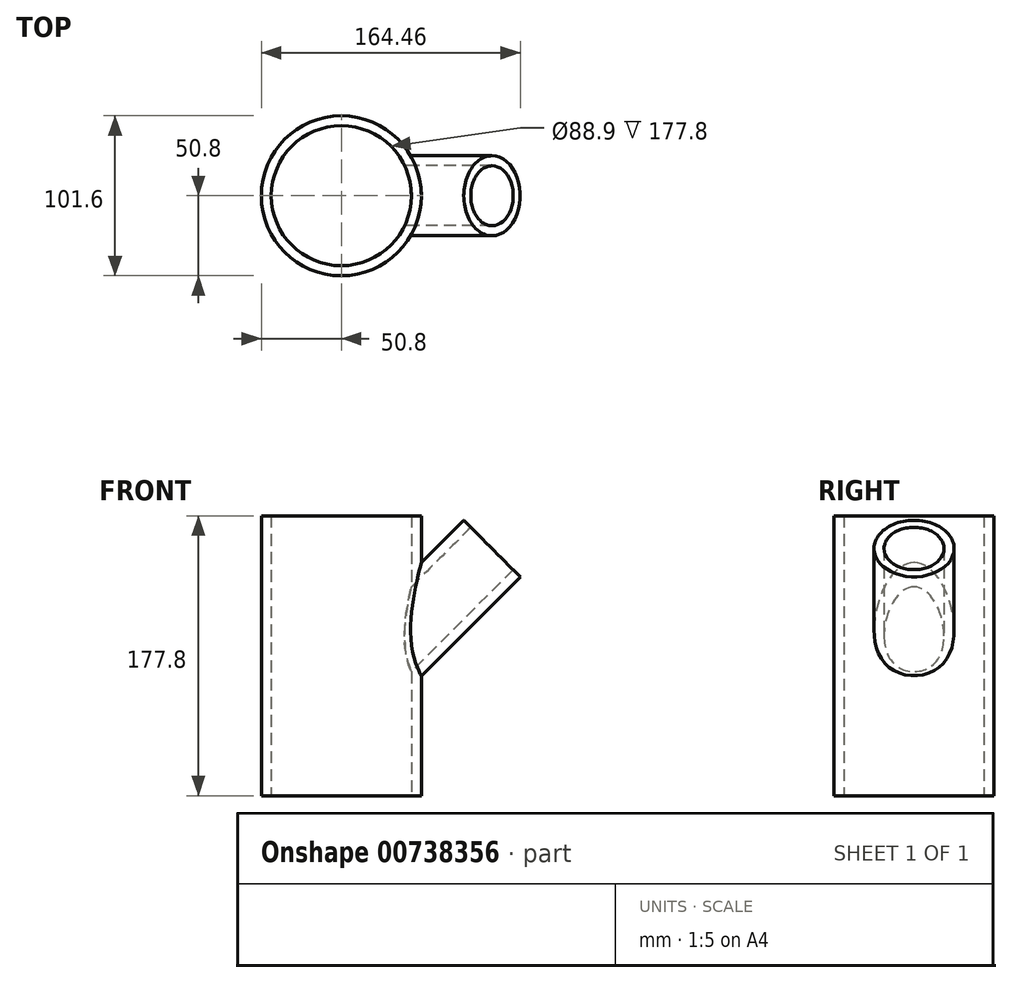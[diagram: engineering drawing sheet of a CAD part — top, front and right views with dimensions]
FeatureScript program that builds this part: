
annotation { "Feature Type Name" : "Feature", "Feature Type Description" : "" }
export const myFeature = defineFeature(function(context is Context, id is Id, definition is map)
    precondition{}
    {
        {
            var Q0;
            Q0=qCreatedBy(makeId("Front.planeOp"),FACE);
            var sketch = newSketch(context, id + "F0", { "sketchPlane" : qUnion([Q0])});
            skLineSegment(sketch, "E0", {"start": v(0, 0) * mm, "end": v(0, 177.8) * mm});
            skLineSegment(sketch, "E1", {"start": v(0, 177.8) * mm, "end": v(50.8, 177.8) * mm});
            skLineSegment(sketch, "E2", {"start": v(50.8, 177.8) * mm, "end": v(50.8, 0) * mm});
            skLineSegment(sketch, "E3", {"start": v(50.8, 0) * mm, "end": v(0, 0) * mm});
            skSolve(sketch);
        }
        {
            var Q0;
            Q0=qSketchRegion(id+"F0",true);
            var Q1;
            Q1=sQuery(id+"F0.wireOp",EDGE,"E0");
            revolve(context, id + "F1", {"entities" : qUnion([Q0]), "axis" : qUnion([Q1]), "revolveType" : RevolveType.FULL, "surfaceOperationType" : NewSurfaceOperationType.NEW});
        }
        {
            var Q0;
            Q0=qCreatedBy(makeId("Front.planeOp"),FACE);
            var sketch = newSketch(context, id + "F2", { "sketchPlane" : qUnion([Q0])});
            skLineSegment(sketch, "E4", {"start": v(0, 61.32) * mm, "end": v(95.7, 157.02) * mm});
            skLineSegment(sketch, "E5", {"start": v(95.7, 157.02) * mm, "end": v(113.66, 139.06) * mm});
            skLineSegment(sketch, "E6", {"start": v(113.66, 139.06) * mm, "end": v(0, 25.4) * mm});
            skLineSegment(sketch, "E7", {"start": v(0, 25.4) * mm, "end": v(0, 61.32) * mm});
            skPoint(sketch, "E8", {"position": v(50.8, 76.2) * mm});
            skSolve(sketch);
        }
        {
            var Q0;
            Q0=qSketchRegion(id+"F2",true);
            var Q1;
            Q1=sQuery(id+"F2.wireOp",EDGE,"E4");
            revolve(context, id + "F3", {"operationType" : NewBodyOperationType.ADD, "entities" : qUnion([Q0]), "axis" : qUnion([Q1]), "revolveType" : RevolveType.FULL, "surfaceOperationType" : NewSurfaceOperationType.NEW});
        }
        {
            var Q0;
            Q0=makeQuery(id+"F1.opRevolve","SWEPT_FACE",FACE,{"disambiguationData":[OSD([sQuery(id+"F0.wireOp",EDGE,"E1")])]});
            var Q1;
            Q1=makeQuery(id+"F3.opRevolve","SWEPT_FACE",FACE,{"disambiguationData":[OSD([sQuery(id+"F2.wireOp",EDGE,"E5")])]});
            var Q2;
            Q2=makeQuery(id+"F1.opRevolve","SWEPT_FACE",FACE,{"disambiguationData":[OSD([sQuery(id+"F0.wireOp",EDGE,"E3")])]});
            shell(context, id + "F4", {"entities" : qUnion([Q0, Q1, Q2]), "thickness" : 6.35 * mm});
        }
    });
